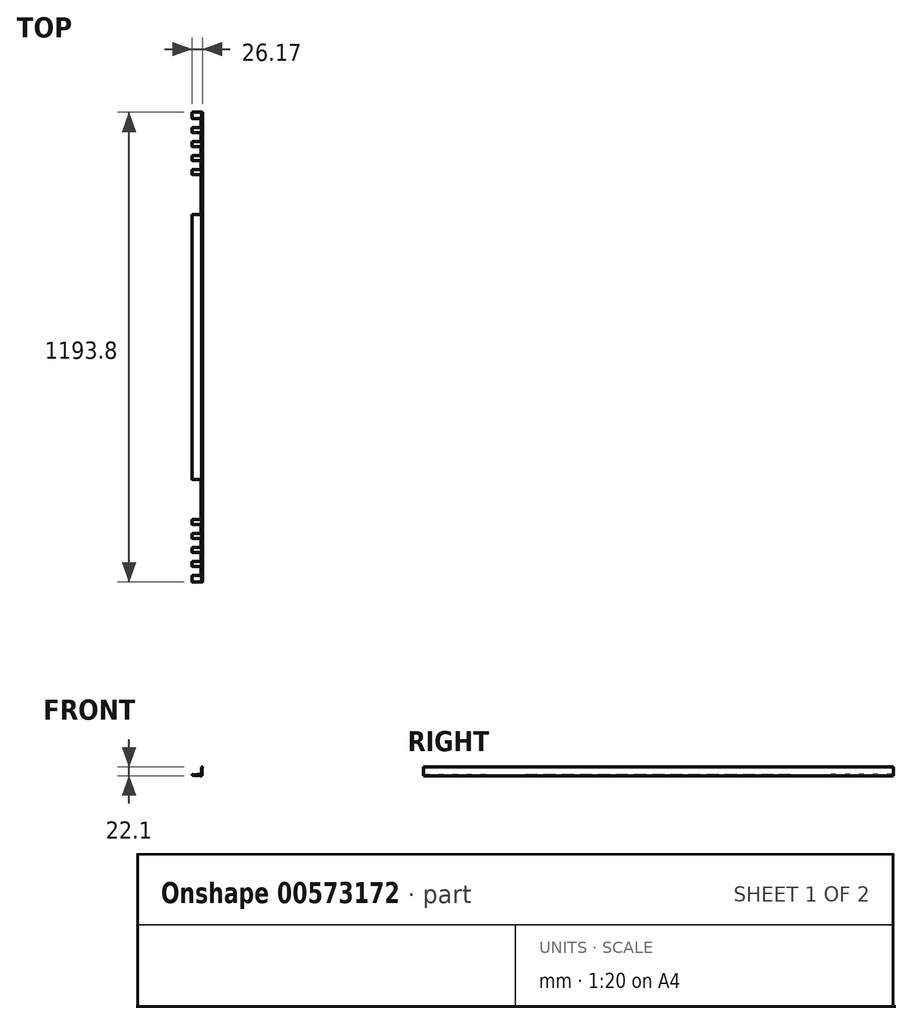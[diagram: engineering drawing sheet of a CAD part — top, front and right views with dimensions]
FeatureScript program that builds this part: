
annotation { "Feature Type Name" : "Feature", "Feature Type Description" : "" }
export const myFeature = defineFeature(function(context is Context, id is Id, definition is map)
    precondition{}
    {
        {
            var Q0;
            Q0=qCreatedBy(makeId("Front.planeOp"),FACE);
            var sketch = newSketch(context, id + "F0", { "sketchPlane" : qUnion([Q0])});
            skLineSegment(sketch, "E0", {"start": v(1.52, 9.1) * mm, "end": v(1.52, 0.76) * mm});
            skLineSegment(sketch, "E1", {"start": v(-0.76, -1.52) * mm, "end": v(-23.88, -1.52) * mm});
            skLineSegment(sketch, "E2", {"start": v(-23.88, -1.52) * mm, "end": v(-23.88, 0) * mm});
            skLineSegment(sketch, "E3", {"start": v(-23.88, 0) * mm, "end": v(-0.76, 0) * mm});
            skLineSegment(sketch, "E4", {"start": v(0, 0.76) * mm, "end": v(0, 9.65) * mm});
            skLineSegment(sketch, "E5", {"start": v(1.52, 11.18) * mm, "end": v(1.52, 11.18) * mm});
            skPoint(sketch, "E6.visualSharp", {"position": v(0, 0) * mm});
            skArc(sketch, "E6.filletArc", {"start": v(-0.76, 0) * mm, "mid": v(-0.22, 0.22) * mm, "end": v(0, 0.76) * mm});
            skPoint(sketch, "E7.visualSharp", {"position": v(1.52, -1.52) * mm});
            skArc(sketch, "E7.filletArc", {"start": v(-0.76, -1.52) * mm, "mid": v(0.85, -0.85) * mm, "end": v(1.52, 0.76) * mm});
            skArc(sketch, "E8", {"start": v(1.9, 9.75) * mm, "mid": v(2.26, 10.61) * mm, "end": v(1.52, 11.18) * mm});
            skPoint(sketch, "E9.visualSharp", {"position": v(0, 11.18) * mm});
            skArc(sketch, "E9.filletArc", {"start": v(1.52, 11.18) * mm, "mid": v(0.45, 10.73) * mm, "end": v(0, 9.65) * mm});
            skArc(sketch, "E10.filletArc", {"start": v(1.9, 9.75) * mm, "mid": v(1.63, 9.48) * mm, "end": v(1.52, 9.1) * mm});
            skSolve(sketch);
        }
        {
            var Q0;
            Q0=qCreatedBy(makeId("Front.planeOp"),FACE);
            var sketch = newSketch(context, id + "F1", { "sketchPlane" : qUnion([Q0])});
            skLineSegment(sketch, "E11", {"start": v(-23.02, 0) * mm, "end": v(-12.7, -1.32) * mm});
            skLineSegment(sketch, "E12", {"start": v(-12.7, -1.32) * mm, "end": v(-12.7, 0) * mm});
            skLineSegment(sketch, "E13", {"start": v(-12.7, 0) * mm, "end": v(-3.3, 0) * mm});
            skLineSegment(sketch, "E14", {"start": v(-3.3, 0) * mm, "end": v(-3.3, -1.52) * mm});
            skLineSegment(sketch, "E15", {"start": v(-3.3, -1.52) * mm, "end": v(0, -1.52) * mm});
            skLineSegment(sketch, "E16", {"start": v(0, -1.52) * mm, "end": v(0, 17.53) * mm});
            skLineSegment(sketch, "E17", {"start": v(1.52, 17.53) * mm, "end": v(1.52, -3.05) * mm});
            skLineSegment(sketch, "E18", {"start": v(1.52, -3.05) * mm, "end": v(-4.83, -3.05) * mm});
            skLineSegment(sketch, "E19", {"start": v(-4.83, -3.05) * mm, "end": v(-4.83, -1.52) * mm});
            skLineSegment(sketch, "E20", {"start": v(-4.83, -1.52) * mm, "end": v(-11.18, -1.52) * mm});
            skLineSegment(sketch, "E21", {"start": v(-11.18, -1.52) * mm, "end": v(-11.18, -3.05) * mm});
            skLineSegment(sketch, "E22", {"start": v(-11.18, -3.05) * mm, "end": v(-23.21, -1.51) * mm});
            skArc(sketch, "E23", {"start": v(-23.02, 0) * mm, "mid": v(-23.87, -0.66) * mm, "end": v(-23.21, -1.51) * mm});
            skArc(sketch, "E24", {"start": v(1.52, 17.53) * mm, "mid": v(2.29, 18.29) * mm, "end": v(1.52, 19.05) * mm});
            skArc(sketch, "E25", {"start": v(1.52, 19.05) * mm, "mid": v(0.45, 18.6) * mm, "end": v(0, 17.53) * mm});
            skSolve(sketch);
        }
        {
            var Q0;
            Q0 = qSketchRegion(id + "F1", true);
            extrude(context, id + "F2", {"entities" : qUnion([Q0]), "depth" : 596.9 * mm, "offsetDistance" : 25.4 * mm});
        }
        {
            var Q0;
            Q0=makeQuery(id+"F2.opExtrude","SWEPT_EDGE",EDGE,{"disambiguationData":[OSD([sQuery(id+"F1.wireOp",EDGE,"E17"),sQuery(id+"F1.wireOp",EDGE,"E24")])]});
            fillet(context, id + "F3", {"entities" : qUnion([Q0]), "radius" : 0.76 * mm, "tangentPropagation" : true, "allowEdgeOverflow" : false});
        }
        {
            var Q0;
            Q0=makeQuery(id+"F2.opExtrude","SWEPT_EDGE",EDGE,{"disambiguationData":[OSD([sQuery(id+"F1.wireOp",EDGE,"E15"),sQuery(id+"F1.wireOp",EDGE,"E16")])]});
            var Q1;
            Q1=makeQuery(id+"F2.opExtrude","SWEPT_EDGE",EDGE,{"disambiguationData":[OSD([sQuery(id+"F1.wireOp",EDGE,"E14"),sQuery(id+"F1.wireOp",EDGE,"E15")])]});
            var Q2;
            Q2=makeQuery(id+"F2.opExtrude","SWEPT_EDGE",EDGE,{"disambiguationData":[OSD([sQuery(id+"F1.wireOp",EDGE,"E11"),sQuery(id+"F1.wireOp",EDGE,"E12")])]});
            var Q3;
            Q3=makeQuery(id+"F2.opExtrude","SWEPT_EDGE",EDGE,{"disambiguationData":[OSD([sQuery(id+"F1.wireOp",EDGE,"E19"),sQuery(id+"F1.wireOp",EDGE,"E20")])]});
            var Q4;
            Q4=makeQuery(id+"F2.opExtrude","SWEPT_EDGE",EDGE,{"disambiguationData":[OSD([sQuery(id+"F1.wireOp",EDGE,"E20"),sQuery(id+"F1.wireOp",EDGE,"E21")])]});
            fillet(context, id + "F4", {"entities" : qUnion([Q0, Q1, Q2, Q3, Q4]), "radius" : 0.76 * mm, "tangentPropagation" : true, "allowEdgeOverflow" : false});
        }
        {
            var Q0;
            Q0=makeQuery(id+"F2.opExtrude","SWEPT_EDGE",EDGE,{"disambiguationData":[OSD([sQuery(id+"F1.wireOp",EDGE,"E21"),sQuery(id+"F1.wireOp",EDGE,"E22")])]});
            var Q1;
            Q1=makeQuery(id+"F2.opExtrude","SWEPT_EDGE",EDGE,{"disambiguationData":[OSD([sQuery(id+"F1.wireOp",EDGE,"E18"),sQuery(id+"F1.wireOp",EDGE,"E19")])]});
            var Q2;
            Q2=makeQuery(id+"F2.opExtrude","SWEPT_EDGE",EDGE,{"disambiguationData":[OSD([sQuery(id+"F1.wireOp",EDGE,"E13"),sQuery(id+"F1.wireOp",EDGE,"E14")])]});
            var Q3;
            Q3=makeQuery(id+"F2.opExtrude","SWEPT_EDGE",EDGE,{"disambiguationData":[OSD([sQuery(id+"F1.wireOp",EDGE,"E12"),sQuery(id+"F1.wireOp",EDGE,"E13")])]});
            var Q4;
            Q4=makeQuery(id+"F2.opExtrude","SWEPT_EDGE",EDGE,{"disambiguationData":[OSD([sQuery(id+"F1.wireOp",EDGE,"E17"),sQuery(id+"F1.wireOp",EDGE,"E18")])]});
            fillet(context, id + "F5", {"entities" : qUnion([Q0, Q1, Q2, Q3, Q4]), "radius" : 2.3 * mm, "tangentPropagation" : true, "allowEdgeOverflow" : false});
        }
        {
            var Q0;
            Q0=qCreatedBy(makeId("Top.planeOp"),FACE);
            cPlane(context, id + "F6", {"entities" : qUnion([Q0]), "cplaneType" : CPlaneType.OFFSET, "offset" : 25.4 * mm, "width" : 152.4 * mm, "height" : 152.4 * mm});
        }
        {
            var Q0;
            Q0=qCreatedBy(id+"F6.planeOp",FACE);
            var sketch = newSketch(context, id + "F7", { "sketchPlane" : qUnion([Q0])});
            skLineSegment(sketch, "E26.bottom", {"start": v(-52.32, -336.55) * mm, "end": v(-1.52, -336.55) * mm});
            skLineSegment(sketch, "E26.top", {"start": v(-52.32, -438.15) * mm, "end": v(-1.52, -438.15) * mm});
            skLineSegment(sketch, "E26.left", {"start": v(-52.32, -336.55) * mm, "end": v(-52.32, -438.15) * mm});
            skLineSegment(sketch, "E26.right", {"start": v(-1.52, -336.55) * mm, "end": v(-1.52, -438.15) * mm});
            skSolve(sketch);
        }
        {
            var Q0;
            Q0 = qSketchRegion(id + "F7", true);
            extrude(context, id + "F8", {"entities" : qUnion([Q0]), "operationType" : NewBodyOperationType.REMOVE, "endBound" : BoundingType.THROUGH_ALL, "oppositeDirection" : true, "depth" : 25.4 * mm, "offsetDistance" : 25.4 * mm});
        }
        {
            var Q0;
            Q0=qCreatedBy(id+"F6.planeOp",FACE);
            var sketch = newSketch(context, id + "F9", { "sketchPlane" : qUnion([Q0])});
            skLineSegment(sketch, "E27.bottom", {"start": v(-52.32, -450.85) * mm, "end": v(-1.52, -450.85) * mm});
            skLineSegment(sketch, "E27.top", {"start": v(-52.32, -473.71) * mm, "end": v(-1.52, -473.71) * mm});
            skLineSegment(sketch, "E27.left", {"start": v(-52.32, -450.85) * mm, "end": v(-52.32, -473.71) * mm});
            skLineSegment(sketch, "E27.right", {"start": v(-1.52, -450.85) * mm, "end": v(-1.52, -473.71) * mm});
            skLineSegment(sketch, "E28.bottom", {"start": v(-52.32, -486.41) * mm, "end": v(-1.52, -486.41) * mm});
            skLineSegment(sketch, "E28.top", {"start": v(-52.32, -509.27) * mm, "end": v(-1.52, -509.27) * mm});
            skLineSegment(sketch, "E28.left", {"start": v(-52.32, -486.41) * mm, "end": v(-52.32, -509.27) * mm});
            skLineSegment(sketch, "E28.right", {"start": v(-1.52, -486.41) * mm, "end": v(-1.52, -509.27) * mm});
            skLineSegment(sketch, "E29.bottom", {"start": v(-52.32, -521.97) * mm, "end": v(-1.52, -521.97) * mm});
            skLineSegment(sketch, "E29.top", {"start": v(-52.32, -544.83) * mm, "end": v(-1.52, -544.83) * mm});
            skLineSegment(sketch, "E29.left", {"start": v(-52.32, -521.97) * mm, "end": v(-52.32, -544.83) * mm});
            skLineSegment(sketch, "E29.right", {"start": v(-1.52, -521.97) * mm, "end": v(-1.52, -544.83) * mm});
            skLineSegment(sketch, "E30.bottom", {"start": v(-52.32, -557.53) * mm, "end": v(-1.52, -557.53) * mm});
            skLineSegment(sketch, "E30.top", {"start": v(-52.32, -580.4) * mm, "end": v(-1.52, -580.4) * mm});
            skLineSegment(sketch, "E30.left", {"start": v(-52.32, -557.53) * mm, "end": v(-52.32, -580.4) * mm});
            skLineSegment(sketch, "E30.right", {"start": v(-1.52, -557.53) * mm, "end": v(-1.52, -580.4) * mm});
            skSolve(sketch);
        }
        {
            var Q0;
            Q0=qSketchRegion(id+"F9",true);
            extrude(context, id + "F10", {"entities" : qUnion([Q0]), "operationType" : NewBodyOperationType.REMOVE, "endBound" : BoundingType.THROUGH_ALL, "oppositeDirection" : true, "depth" : 25.4 * mm, "offsetDistance" : 25.4 * mm});
        }
        {
            var Q0;
            Q0=makeQuery(id+"F8.boolean.opBoolean","COPY",EDGE,{"derivedFrom":makeQuery(id+"F8.opExtrude","SWEPT_EDGE",EDGE,{"disambiguationData":[OSD([sQuery(id+"F7.wireOp",EDGE,"E26.bottom"),sQuery(id+"F7.wireOp",EDGE,"E26.right")])]})});
            var Q1;
            Q1=makeQuery(id+"F8.boolean.opBoolean","COPY",EDGE,{"derivedFrom":makeQuery(id+"F8.opExtrude","SWEPT_EDGE",EDGE,{"disambiguationData":[OSD([sQuery(id+"F7.wireOp",EDGE,"E26.top"),sQuery(id+"F7.wireOp",EDGE,"E26.right")])]})});
            var Q2;
            Q2=makeQuery(id+"F10.boolean.opBoolean","COPY",EDGE,{"derivedFrom":makeQuery(id+"F10.opExtrude","SWEPT_EDGE",EDGE,{"disambiguationData":[OSD([sQuery(id+"F9.wireOp",EDGE,"E27.bottom"),sQuery(id+"F9.wireOp",EDGE,"E27.right")])]})});
            var Q3;
            Q3=makeQuery(id+"F10.boolean.opBoolean","COPY",EDGE,{"derivedFrom":makeQuery(id+"F10.opExtrude","SWEPT_EDGE",EDGE,{"disambiguationData":[OSD([sQuery(id+"F9.wireOp",EDGE,"E27.top"),sQuery(id+"F9.wireOp",EDGE,"E27.right")])]})});
            var Q4;
            Q4=makeQuery(id+"F10.boolean.opBoolean","COPY",EDGE,{"derivedFrom":makeQuery(id+"F10.opExtrude","SWEPT_EDGE",EDGE,{"disambiguationData":[OSD([sQuery(id+"F9.wireOp",EDGE,"E28.top"),sQuery(id+"F9.wireOp",EDGE,"E28.right")])]})});
            var Q5;
            Q5=makeQuery(id+"F10.boolean.opBoolean","COPY",EDGE,{"derivedFrom":makeQuery(id+"F10.opExtrude","SWEPT_EDGE",EDGE,{"disambiguationData":[OSD([sQuery(id+"F9.wireOp",EDGE,"E29.top"),sQuery(id+"F9.wireOp",EDGE,"E29.right")])]})});
            var Q6;
            Q6=makeQuery(id+"F10.boolean.opBoolean","COPY",EDGE,{"derivedFrom":makeQuery(id+"F10.opExtrude","SWEPT_EDGE",EDGE,{"disambiguationData":[OSD([sQuery(id+"F9.wireOp",EDGE,"E30.top"),sQuery(id+"F9.wireOp",EDGE,"E30.right")])]})});
            var Q7;
            Q7=makeQuery(id+"F10.boolean.opBoolean","COPY",EDGE,{"derivedFrom":makeQuery(id+"F10.opExtrude","SWEPT_EDGE",EDGE,{"disambiguationData":[OSD([sQuery(id+"F9.wireOp",EDGE,"E28.bottom"),sQuery(id+"F9.wireOp",EDGE,"E28.right")])]})});
            var Q8;
            Q8=makeQuery(id+"F10.boolean.opBoolean","COPY",EDGE,{"derivedFrom":makeQuery(id+"F10.opExtrude","SWEPT_EDGE",EDGE,{"disambiguationData":[OSD([sQuery(id+"F9.wireOp",EDGE,"E29.bottom"),sQuery(id+"F9.wireOp",EDGE,"E29.right")])]})});
            var Q9;
            Q9=makeQuery(id+"F10.boolean.opBoolean","COPY",EDGE,{"derivedFrom":makeQuery(id+"F10.opExtrude","SWEPT_EDGE",EDGE,{"disambiguationData":[OSD([sQuery(id+"F9.wireOp",EDGE,"E30.bottom"),sQuery(id+"F9.wireOp",EDGE,"E30.right")])]})});
            fillet(context, id + "F11", {"entities" : qUnion([Q0, Q1, Q2, Q3, Q4, Q5, Q6, Q7, Q8, Q9]), "radius" : 3.17 * mm, "tangentPropagation" : true, "allowEdgeOverflow" : false});
        }
        {
            var Q0;
            Q0=makeQuery(id+"F2.opExtrude","SWEPT_BODY",BODY,{"disambiguationData":[OSD([sQuery(id+"F1.wireOp",EDGE,"E11"),sQuery(id+"F1.wireOp",EDGE,"E12"),sQuery(id+"F1.wireOp",EDGE,"E13"),sQuery(id+"F1.wireOp",EDGE,"E14"),sQuery(id+"F1.wireOp",EDGE,"E15"),sQuery(id+"F1.wireOp",EDGE,"E16"),sQuery(id+"F1.wireOp",EDGE,"E17"),sQuery(id+"F1.wireOp",EDGE,"E18"),sQuery(id+"F1.wireOp",EDGE,"E19"),sQuery(id+"F1.wireOp",EDGE,"E20"),sQuery(id+"F1.wireOp",EDGE,"E21"),sQuery(id+"F1.wireOp",EDGE,"E22"),sQuery(id+"F1.wireOp",EDGE,"E23"),sQuery(id+"F1.wireOp",EDGE,"E24"),sQuery(id+"F1.wireOp",EDGE,"E25")])]});
            var Q1;
            Q1=qCreatedBy(makeId("Front.planeOp"),FACE);
            mirror(context, id + "F12", {"operationType" : NewBodyOperationType.ADD, "entities" : qUnion([Q0]), "mirrorPlane" : qUnion([Q1])});
        }
    });
